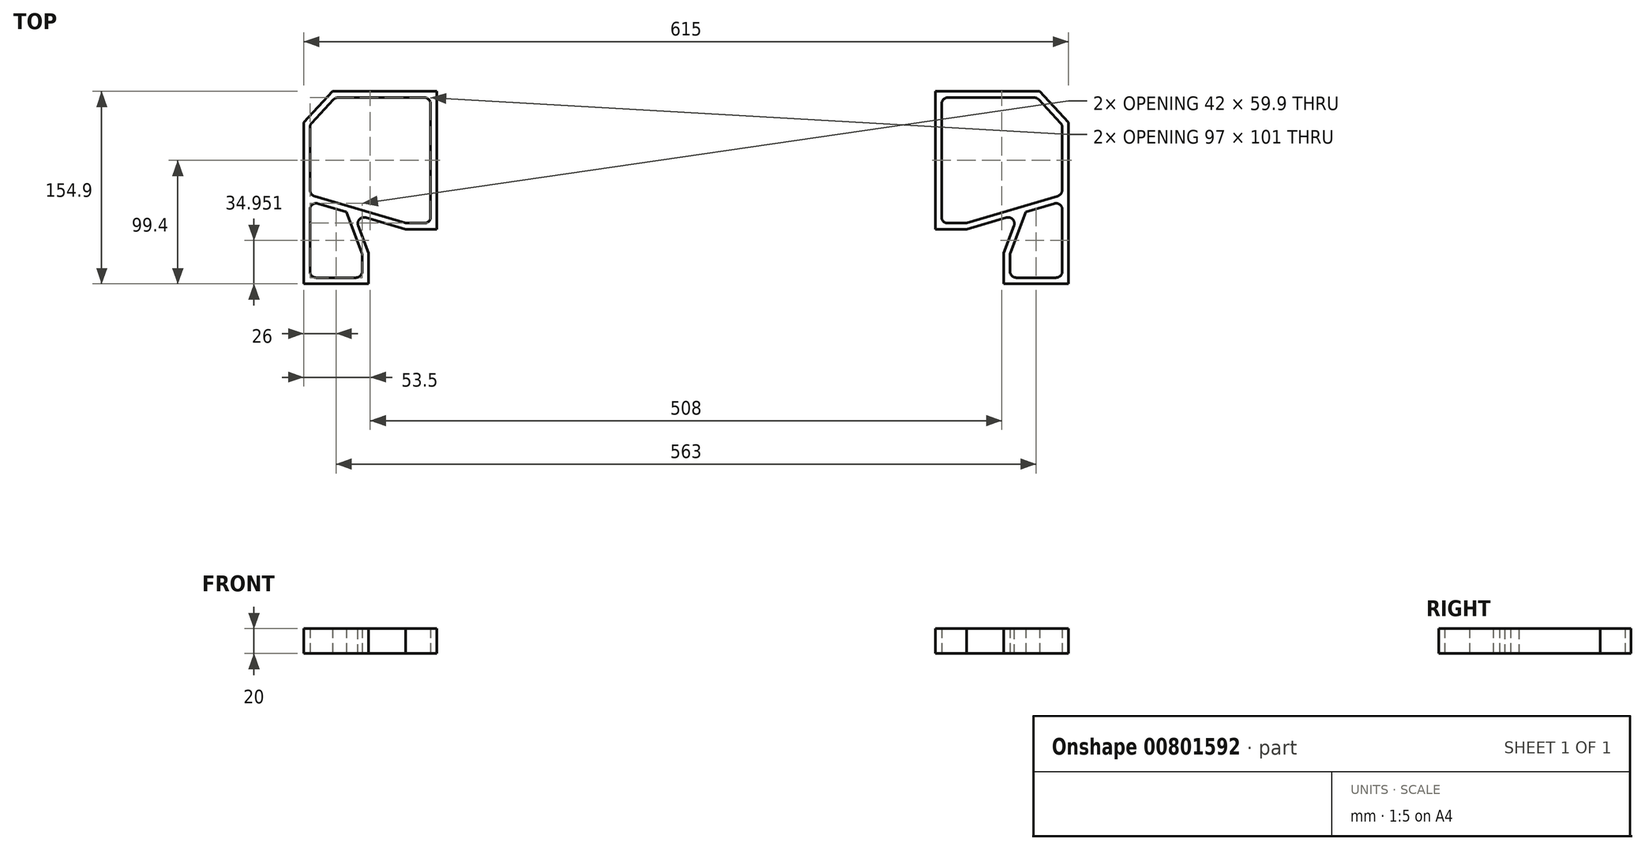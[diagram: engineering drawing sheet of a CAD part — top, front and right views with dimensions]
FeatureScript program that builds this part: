
annotation { "Feature Type Name" : "Feature", "Feature Type Description" : "" }
export const myFeature = defineFeature(function(context is Context, id is Id, definition is map)
    precondition{}
    {
        {
            var Q0;
            Q0=qCreatedBy(makeId("Top.planeOp"),FACE);
            var sketch = newSketch(context, id + "F0", { "sketchPlane" : qUnion([Q0])});
            skLineSegment(sketch, "E0.bottom", {"start": v(307.5, -227) * mm, "end": v(-307.5, -227) * mm, "construction": true});
            skLineSegment(sketch, "E0.top", {"start": v(307.5, 227) * mm, "end": v(-307.5, 227) * mm, "construction": true});
            skLineSegment(sketch, "E0.left", {"start": v(307.5, -227) * mm, "end": v(307.5, 227) * mm, "construction": true});
            skLineSegment(sketch, "E0.right", {"start": v(-307.5, -227) * mm, "end": v(-307.5, 227) * mm, "construction": true});
            skPoint(sketch, "E0.middle", {"position": v(0, 0) * mm});
            skLineSegment(sketch, "E1", {"start": v(0, -227) * mm, "end": v(255.5, -227) * mm, "construction": true});
            skLineSegment(sketch, "E2", {"start": v(255.5, -227) * mm, "end": v(255.5, 116) * mm, "construction": true});
            skLineSegment(sketch, "E3", {"start": v(255.5, 116) * mm, "end": v(-255.5, 116) * mm, "construction": true});
            skLineSegment(sketch, "E4", {"start": v(-255.5, 116) * mm, "end": v(-255.5, -227) * mm, "construction": true});
            skLineSegment(sketch, "E5", {"start": v(-255.5, -227) * mm, "end": v(0, -227) * mm, "construction": true});
            skLineSegment(sketch, "E6", {"start": v(-255.5, 116) * mm, "end": v(-225.5, 116) * mm, "construction": true});
            skLineSegment(sketch, "E7", {"start": v(-225.5, 116) * mm, "end": v(-200.5, 116) * mm});
            skLineSegment(sketch, "E8", {"start": v(-200.5, 116) * mm, "end": v(-200.5, 227) * mm});
            skLineSegment(sketch, "E9", {"start": v(-200.5, 227) * mm, "end": v(-284.35, 227) * mm});
            skLineSegment(sketch, "E10", {"start": v(-284.35, 227) * mm, "end": v(-307.5, 202.1) * mm});
            skLineSegment(sketch, "E11", {"start": v(-307.5, 202.1) * mm, "end": v(-307.5, 72.1) * mm});
            skLineSegment(sketch, "E12", {"start": v(-307.5, 72.1) * mm, "end": v(-255.5, 72.1) * mm});
            skLineSegment(sketch, "E13", {"start": v(-255.5, 72.1) * mm, "end": v(-255.5, 97.1) * mm});
            skLineSegment(sketch, "E14", {"start": v(-255.5, 97.1) * mm, "end": v(-267.23, 128.3) * mm});
            skLineSegment(sketch, "E15", {"start": v(-267.23, 128.3) * mm, "end": v(-225.5, 116) * mm});
            skLineSegment(sketch, "E16.0", {"start": v(-205.5, 121) * mm, "end": v(-205.5, 222) * mm});
            skLineSegment(sketch, "E17.0", {"start": v(-282.18, 222) * mm, "end": v(-302.5, 200.14) * mm});
            skLineSegment(sketch, "E18.0", {"start": v(-205.5, 222) * mm, "end": v(-282.18, 222) * mm});
            skLineSegment(sketch, "E19.0", {"start": v(-224.78, 121) * mm, "end": v(-205.5, 121) * mm});
            skLineSegment(sketch, "E20.0", {"start": v(-302.5, 143.9) * mm, "end": v(-224.78, 121) * mm});
            skLineSegment(sketch, "E21.0", {"start": v(-260.5, 96.2) * mm, "end": v(-273.25, 130.09) * mm});
            skLineSegment(sketch, "E22.0", {"start": v(-260.5, 77.1) * mm, "end": v(-260.5, 96.2) * mm});
            skLineSegment(sketch, "E23.0", {"start": v(-302.5, 77.1) * mm, "end": v(-260.5, 77.1) * mm});
            skLineSegment(sketch, "E24.0", {"start": v(-302.5, 200.14) * mm, "end": v(-302.5, 143.9) * mm});
            skLineSegment(sketch, "E25", {"start": v(-273.24, 130.07) * mm, "end": v(-302.5, 138.7) * mm});
            skLineSegment(sketch, "E26.trimOffspring", {"start": v(-302.5, 138.7) * mm, "end": v(-302.5, 77.1) * mm});
            skLineSegment(sketch, "E27", {"start": v(0, 0) * mm, "end": v(0, 201.7) * mm, "construction": true});
            skSolve(sketch);
        }
        {
            var Q0;
            Q0=makeQuery(id+"F0.imprint","IMPRINT",FACE,{"disambiguationData":[TD([[makeQuery(id+"F0.imprint","IMPRINT",EDGE,{"derivedFrom":sQuery(id+"F0.wireOp",EDGE,"E7")}),1.0]])]});
            extrude(context, id + "F1", {"entities" : qUnion([Q0]), "depth" : 20 * mm, "offsetDistance" : 25 * mm});
        }
        {
            var Q0;
            Q0=makeQuery(id+"F1.opExtrude","SWEPT_EDGE",EDGE,{"disambiguationData":[OSD([sQuery(id+"F0.wireOp",EDGE,"E14"),sQuery(id+"F0.wireOp",EDGE,"E15")])]});
            var Q1;
            Q1=makeQuery(id+"F1.opExtrude","SWEPT_EDGE",EDGE,{"disambiguationData":[OSD([sQuery(id+"F0.wireOp",EDGE,"E16.0"),sQuery(id+"F0.wireOp",EDGE,"E19.0")])]});
            var Q2;
            Q2=makeQuery(id+"F1.opExtrude","SWEPT_EDGE",EDGE,{"disambiguationData":[OSD([sQuery(id+"F0.wireOp",EDGE,"E21.0"),sQuery(id+"F0.wireOp",EDGE,"E22.0")])]});
            var Q3;
            Q3=makeQuery(id+"F1.opExtrude","SWEPT_EDGE",EDGE,{"disambiguationData":[OSD([sQuery(id+"F0.wireOp",EDGE,"E22.0"),sQuery(id+"F0.wireOp",EDGE,"E23.0")])]});
            var Q4;
            Q4=makeQuery(id+"F1.opExtrude","SWEPT_EDGE",EDGE,{"disambiguationData":[OSD([sQuery(id+"F0.wireOp",EDGE,"E19.0"),sQuery(id+"F0.wireOp",EDGE,"E20.0")])]});
            var Q5;
            Q5=makeQuery(id+"F1.opExtrude","SWEPT_EDGE",EDGE,{"disambiguationData":[OSD([sQuery(id+"F0.wireOp",EDGE,"E17.0"),sQuery(id+"F0.wireOp",EDGE,"E18.0")])]});
            var Q6;
            Q6=makeQuery(id+"F1.opExtrude","SWEPT_EDGE",EDGE,{"disambiguationData":[OSD([sQuery(id+"F0.wireOp",EDGE,"E17.0"),sQuery(id+"F0.wireOp",EDGE,"E24.0")])]});
            var Q7;
            Q7=makeQuery(id+"F1.opExtrude","SWEPT_EDGE",EDGE,{"disambiguationData":[OSD([sQuery(id+"F0.wireOp",EDGE,"E25"),sQuery(id+"F0.wireOp",EDGE,"E26.trimOffspring")])]});
            var Q8;
            Q8=makeQuery(id+"F1.opExtrude","SWEPT_EDGE",EDGE,{"disambiguationData":[OSD([sQuery(id+"F0.wireOp",EDGE,"E23.0"),sQuery(id+"F0.wireOp",EDGE,"E26.trimOffspring")])]});
            var Q9;
            Q9=makeQuery(id+"F1.opExtrude","SWEPT_EDGE",EDGE,{"disambiguationData":[OSD([sQuery(id+"F0.wireOp",EDGE,"E20.0"),sQuery(id+"F0.wireOp",EDGE,"E24.0")])]});
            var Q10;
            Q10=makeQuery(id+"F1.opExtrude","SWEPT_EDGE",EDGE,{"disambiguationData":[OSD([sQuery(id+"F0.wireOp",EDGE,"E16.0"),sQuery(id+"F0.wireOp",EDGE,"E18.0")])]});
            fillet(context, id + "F2", {"entities" : qUnion([Q0, Q1, Q2, Q3, Q4, Q5, Q6, Q7, Q8, Q9, Q10]), "radius" : 5 * mm, "tangentPropagation" : true, "allowEdgeOverflow" : false});
        }
        {
            var Q0;
            Q0=makeQuery(id+"F1.opExtrude","SWEPT_BODY",BODY,{"disambiguationData":[OSD([sQuery(id+"F0.wireOp",EDGE,"E7"),sQuery(id+"F0.wireOp",EDGE,"E8"),sQuery(id+"F0.wireOp",EDGE,"E9"),sQuery(id+"F0.wireOp",EDGE,"E10"),sQuery(id+"F0.wireOp",EDGE,"E11"),sQuery(id+"F0.wireOp",EDGE,"E12"),sQuery(id+"F0.wireOp",EDGE,"E13"),sQuery(id+"F0.wireOp",EDGE,"E14"),sQuery(id+"F0.wireOp",EDGE,"E15"),sQuery(id+"F0.wireOp",EDGE,"E16.0"),sQuery(id+"F0.wireOp",EDGE,"E17.0"),sQuery(id+"F0.wireOp",EDGE,"E18.0"),sQuery(id+"F0.wireOp",EDGE,"E19.0"),sQuery(id+"F0.wireOp",EDGE,"E20.0"),sQuery(id+"F0.wireOp",EDGE,"E21.0"),sQuery(id+"F0.wireOp",EDGE,"E22.0"),sQuery(id+"F0.wireOp",EDGE,"E23.0"),sQuery(id+"F0.wireOp",EDGE,"E24.0"),sQuery(id+"F0.wireOp",EDGE,"E25"),sQuery(id+"F0.wireOp",EDGE,"E26.trimOffspring")])]});
            var Q1;
            Q1=qCreatedBy(makeId("Right.planeOp"),FACE);
            mirror(context, id + "F3", {"entities" : qUnion([Q0]), "mirrorPlane" : qUnion([Q1])});
        }
    });
